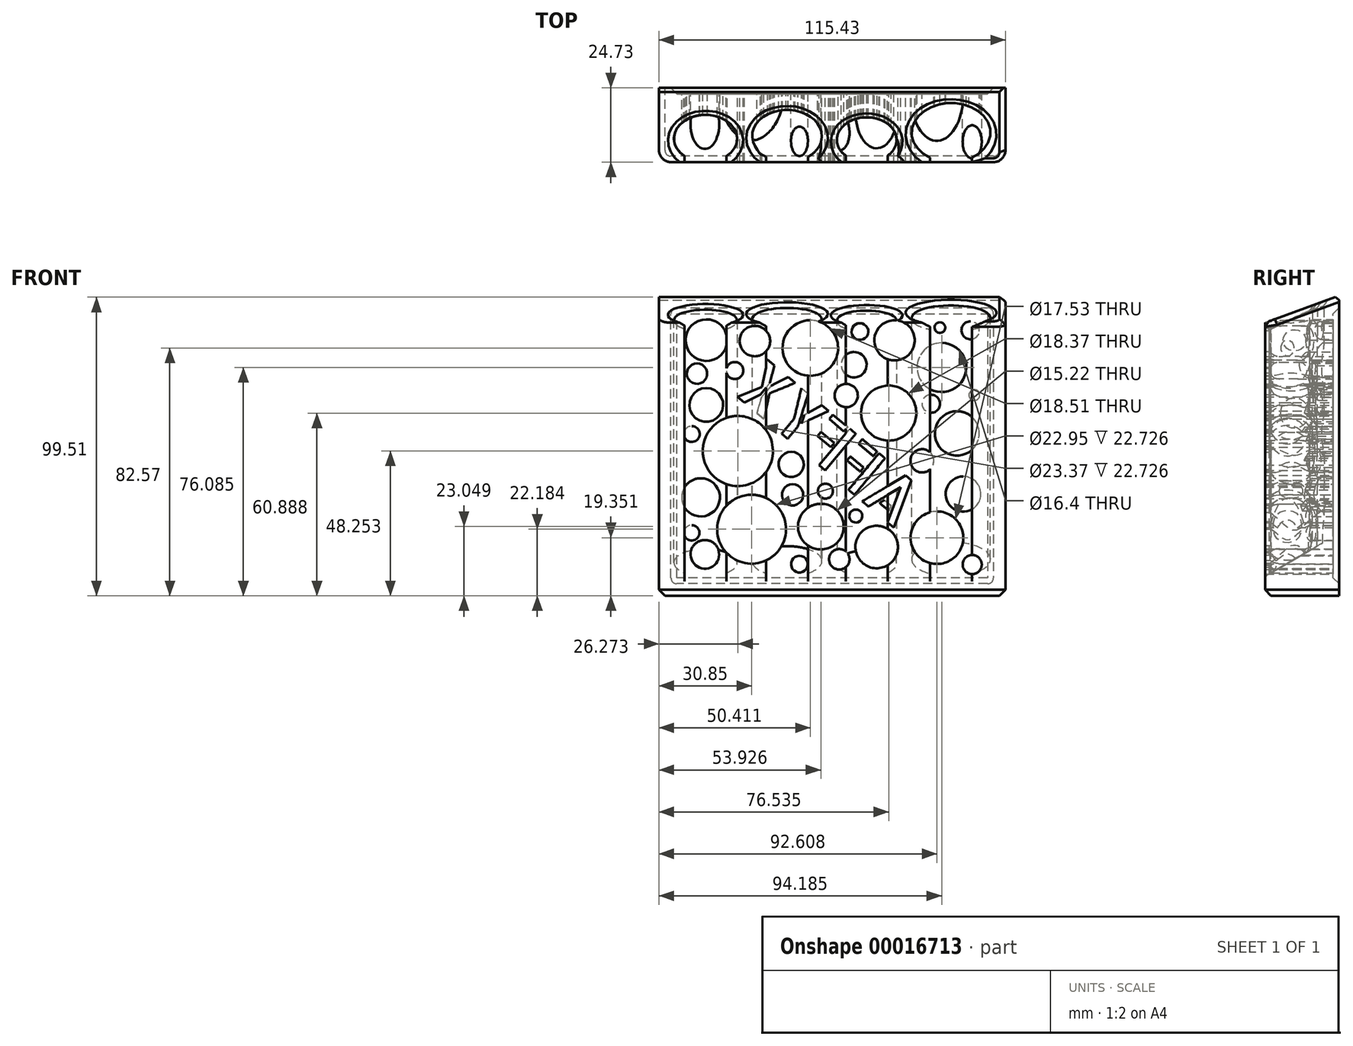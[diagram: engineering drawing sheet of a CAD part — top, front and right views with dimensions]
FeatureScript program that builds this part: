
annotation { "Feature Type Name" : "Feature", "Feature Type Description" : "" }
export const myFeature = defineFeature(function(context is Context, id is Id, definition is map)
    precondition{}
    {
        {
            var Q0;
            Q0=qCreatedBy(makeId("Top.planeOp"),FACE);
            var sketch = newSketch(context, id + "F0", { "sketchPlane" : qUnion([Q0])});
            skEllipse(sketch, "E0", {"center": v(15.53, 7.9) * mm, "majorRadius": 10.53 * mm, "minorRadius": 7.9 * mm, "majorAxis": v(1, 0)});
            skEllipse(sketch, "E1", {"center": v(42.66, 8.7) * mm, "majorRadius": 11.6 * mm, "minorRadius": 8.7 * mm, "majorAxis": v(1, 0)});
            skEllipse(sketch, "E2", {"center": v(69.22, 7.47) * mm, "majorRadius": 9.96 * mm, "minorRadius": 7.47 * mm, "majorAxis": v(-1, 0)});
            skEllipse(sketch, "E3", {"center": v(97.3, 9.85) * mm, "majorRadius": 13.13 * mm, "minorRadius": 9.85 * mm, "majorAxis": v(-1, 0)});
            skLineSegment(sketch, "E4", {"start": v(0, 0) * mm, "end": v(120, 0) * mm, "construction": true});
            skSolve(sketch);
        }
        {
            var Q0;
            Q0=qCreatedBy(makeId("Top.planeOp"),FACE);
            var sketch = newSketch(context, id + "F1", { "sketchPlane" : qUnion([Q0])});
            skLineSegment(sketch, "E5.bottom", {"start": v(8.53, -4.1) * mm, "end": v(22.52, -4.1) * mm});
            skLineSegment(sketch, "E5.top", {"start": v(8.53, 7.9) * mm, "end": v(22.52, 7.9) * mm});
            skLineSegment(sketch, "E5.left", {"start": v(8.53, -4.1) * mm, "end": v(8.53, 7.9) * mm});
            skLineSegment(sketch, "E5.right", {"start": v(22.53, -4.1) * mm, "end": v(22.53, 7.9) * mm});
            skLineSegment(sketch, "E6.bottom", {"start": v(35.66, -3.3) * mm, "end": v(49.66, -3.3) * mm});
            skLineSegment(sketch, "E6.top", {"start": v(35.66, 8.7) * mm, "end": v(49.66, 8.7) * mm});
            skLineSegment(sketch, "E6.left", {"start": v(35.66, -3.3) * mm, "end": v(35.66, 8.7) * mm});
            skLineSegment(sketch, "E6.right", {"start": v(49.66, -3.3) * mm, "end": v(49.66, 8.7) * mm});
            skLineSegment(sketch, "E7.bottom", {"start": v(62.22, -4.53) * mm, "end": v(76.22, -4.53) * mm});
            skLineSegment(sketch, "E7.top", {"start": v(62.22, 7.47) * mm, "end": v(76.22, 7.47) * mm});
            skLineSegment(sketch, "E7.left", {"start": v(62.22, -4.53) * mm, "end": v(62.22, 7.47) * mm});
            skLineSegment(sketch, "E7.right", {"start": v(76.22, -4.53) * mm, "end": v(76.22, 7.47) * mm});
            skLineSegment(sketch, "E8.bottom", {"start": v(90.3, -2.15) * mm, "end": v(104.3, -2.15) * mm});
            skLineSegment(sketch, "E8.top", {"start": v(90.3, 9.85) * mm, "end": v(104.3, 9.85) * mm});
            skLineSegment(sketch, "E8.left", {"start": v(90.3, -2.15) * mm, "end": v(90.3, 9.85) * mm});
            skLineSegment(sketch, "E8.right", {"start": v(104.3, -2.15) * mm, "end": v(104.3, 9.85) * mm});
            skSolve(sketch);
        }
        {
            var Q0;
            Q0=qCreatedBy(makeId("Top.planeOp"),FACE);
            var sketch = newSketch(context, id + "F2", { "sketchPlane" : qUnion([Q0])});
            skLineSegment(sketch, "E9.bottom", {"start": v(0, 0) * mm, "end": v(115.43, 0) * mm});
            skLineSegment(sketch, "E9.top", {"start": v(0, 24.73) * mm, "end": v(115.43, 24.73) * mm});
            skLineSegment(sketch, "E9.left", {"start": v(0, 0) * mm, "end": v(0, 24.73) * mm});
            skLineSegment(sketch, "E9.right", {"start": v(115.43, 0) * mm, "end": v(115.43, 24.73) * mm});
            skSolve(sketch);
        }
        {
            var Q0;
            Q0=makeQuery(id+"F2.imprint","IMPRINT",FACE,{"disambiguationData":[TD([[makeQuery(id+"F2.imprint","IMPRINT",EDGE,{"derivedFrom":sQuery(id+"F2.wireOp",EDGE,"E9.bottom")}),1.0]])]});
            extrude(context, id + "F3", {"entities" : qUnion([Q0]), "oppositeDirection" : true, "depth" : 100 * mm});
        }
        {
            var Q0;
            Q0 = qSketchRegion(id + "F1", true);
            extrude(context, id + "F4", {"entities" : qUnion([Q0]), "operationType" : NewBodyOperationType.REMOVE, "oppositeDirection" : true, "depth" : 95 * mm});
        }
        {
            var Q0;
            Q0 = qSketchRegion(id + "F0", true);
            extrude(context, id + "F5", {"entities" : qUnion([Q0]), "operationType" : NewBodyOperationType.REMOVE, "oppositeDirection" : true, "depth" : 95 * mm});
        }
        {
            var Q0;
            Q0=makeQuery(id+"F3.opExtrude","SWEPT_FACE",FACE,{"disambiguationData":[OSD([sQuery(id+"F2.wireOp",EDGE,"E9.right")])]});
            var sketch = newSketch(context, id + "F6", { "sketchPlane" : qUnion([Q0])});
            skLineSegment(sketch, "E10", {"start": v(0, -100) * mm, "end": v(0, -93.5) * mm});
            skLineSegment(sketch, "E11", {"start": v(0, -93.5) * mm, "end": v(24.73, -79.22) * mm});
            skLineSegment(sketch, "E12", {"start": v(24.73, -79.22) * mm, "end": v(24.73, -100) * mm});
            skLineSegment(sketch, "E13", {"start": v(24.73, -100) * mm, "end": v(0, -100) * mm});
            skSolve(sketch);
        }
        {
            var Q0;
            Q0 = qSketchRegion(id + "F6", true);
            var Q1;
            Q1=makeQuery(id+"F3.opExtrude","SWEPT_FACE",FACE,{"disambiguationData":[OSD([sQuery(id+"F2.wireOp",EDGE,"E9.left")])]});
            extrude(context, id + "F7", {"entities" : qUnion([Q0]), "operationType" : NewBodyOperationType.ADD, "endBound" : BoundingType.UP_TO_SURFACE, "oppositeDirection" : true, "endBoundEntityFace" : qUnion([Q1]), "depth" : 25 * mm});
        }
        {
            var Q0;
            Q0=makeQuery(id+"F3.opExtrude","SWEPT_FACE",FACE,{"disambiguationData":[OSD([sQuery(id+"F2.wireOp",EDGE,"E9.left")])]});
            var sketch = newSketch(context, id + "F8", { "sketchPlane" : qUnion([Q0])});
            skLineSegment(sketch, "E14", {"start": v(0, 0) * mm, "end": v(-24.73, 0) * mm});
            skLineSegment(sketch, "E15", {"start": v(-24.73, 0) * mm, "end": v(0, -9) * mm});
            skLineSegment(sketch, "E16", {"start": v(0, -9) * mm, "end": v(0, 0) * mm});
            skSolve(sketch);
        }
        {
            var Q0;
            Q0=makeQuery(id+"F8.imprint","IMPRINT",FACE,{"disambiguationData":[TD([[makeQuery(id+"F8.imprint","IMPRINT",EDGE,{"derivedFrom":sQuery(id+"F8.wireOp",EDGE,"E14")}),1.0]])]});
            extrude(context, id + "F9", {"entities" : qUnion([Q0]), "operationType" : NewBodyOperationType.REMOVE, "endBound" : BoundingType.THROUGH_ALL, "oppositeDirection" : true, "depth" : 25 * mm});
        }
        {
            var Q0;
            Q0=makeQuery(id+"F3.opExtrude","SWEPT_EDGE",EDGE,{"disambiguationData":[OSD([sQuery(id+"F2.wireOp",EDGE,"E9.bottom"),sQuery(id+"F2.wireOp",EDGE,"E9.right")])]});
            var Q1;
            Q1=makeQuery(id+"F9.boolean.opBoolean","COPY",EDGE,{"disambiguationData":[OD(1.0)],"derivedFrom":makeQuery(id+"F9.opExtrude","SWEPT_EDGE",EDGE,{"disambiguationData":[OSD([sQuery(id+"F2.wireOp",EDGE,"E9.bottom"),sQuery(id+"F2.wireOp",EDGE,"E9.left"),sQuery(id+"F8.wireOp",EDGE,"E15"),sQuery(id+"F8.wireOp",EDGE,"E16")])]})});
            var Q2;
            Q2=makeQuery(id+"F9.boolean.opBoolean","COPY",EDGE,{"disambiguationData":[OD(4.0)],"derivedFrom":makeQuery(id+"F9.opExtrude","SWEPT_EDGE",EDGE,{"disambiguationData":[OSD([sQuery(id+"F2.wireOp",EDGE,"E9.bottom"),sQuery(id+"F2.wireOp",EDGE,"E9.left"),sQuery(id+"F8.wireOp",EDGE,"E15"),sQuery(id+"F8.wireOp",EDGE,"E16")])]})});
            var Q3;
            Q3=makeQuery(id+"F9.boolean.opBoolean","COPY",EDGE,{"disambiguationData":[OD(3.0)],"derivedFrom":makeQuery(id+"F9.opExtrude","SWEPT_EDGE",EDGE,{"disambiguationData":[OSD([sQuery(id+"F2.wireOp",EDGE,"E9.bottom"),sQuery(id+"F2.wireOp",EDGE,"E9.left"),sQuery(id+"F8.wireOp",EDGE,"E15"),sQuery(id+"F8.wireOp",EDGE,"E16")])]})});
            var Q4;
            Q4=makeQuery(id+"F9.boolean.opBoolean","COPY",EDGE,{"disambiguationData":[OD(2.0)],"derivedFrom":makeQuery(id+"F9.opExtrude","SWEPT_EDGE",EDGE,{"disambiguationData":[OSD([sQuery(id+"F2.wireOp",EDGE,"E9.bottom"),sQuery(id+"F2.wireOp",EDGE,"E9.left"),sQuery(id+"F8.wireOp",EDGE,"E15"),sQuery(id+"F8.wireOp",EDGE,"E16")])]})});
            var Q5;
            Q5=makeQuery(id+"F9.boolean.opBoolean","COPY",EDGE,{"disambiguationData":[OD(0.0)],"derivedFrom":makeQuery(id+"F9.opExtrude","SWEPT_EDGE",EDGE,{"disambiguationData":[OSD([sQuery(id+"F2.wireOp",EDGE,"E9.bottom"),sQuery(id+"F2.wireOp",EDGE,"E9.left"),sQuery(id+"F8.wireOp",EDGE,"E15"),sQuery(id+"F8.wireOp",EDGE,"E16")])]})});
            var Q6;
            Q6=makeQuery(id+"F3.opExtrude","SWEPT_EDGE",EDGE,{"disambiguationData":[OSD([sQuery(id+"F2.wireOp",EDGE,"E9.bottom"),sQuery(id+"F2.wireOp",EDGE,"E9.left")])]});
            fillet(context, id + "F10", {"entities" : qUnion([Q0, Q1, Q2, Q3, Q4, Q5, Q6]), "radius" : 4 * mm, "allowEdgeOverflow" : false});
        }
        {
            var Q0;
            Q0=makeQuery(id+"F9.boolean.opBoolean","COPY",EDGE,{"derivedFrom":makeQuery(id+"F9.opExtrude","CAP_EDGE",EDGE,{"disambiguationData":[OSD([sQuery(id+"F8.wireOp",EDGE,"E15")])],"isStart":true})});
            var Q1;
            Q1=makeQuery(id+"F9.boolean.opBoolean","INTERSECT",EDGE,{"derivedFrom":[makeQuery(id+"F3.opExtrude","SWEPT_FACE",FACE,{"disambiguationData":[OSD([sQuery(id+"F2.wireOp",EDGE,"E9.right")])]}),makeQuery(id+"F9.opExtrude","SWEPT_FACE",FACE,{"disambiguationData":[OSD([sQuery(id+"F8.wireOp",EDGE,"E15")])]})]});
            var Q2;
            Q2=makeQuery(id+"F3.opExtrude","CAP_EDGE",EDGE,{"disambiguationData":[OSD([sQuery(id+"F2.wireOp",EDGE,"E9.bottom")])],"isStart":false});
            var Q3;
            Q3=makeQuery(id+"F9.boolean.opBoolean","INTERSECT",EDGE,{"derivedFrom":[makeQuery(id+"F5.boolean.opBoolean","COPY",FACE,{"derivedFrom":makeQuery(id+"F5.opExtrude","SWEPT_FACE",FACE,{"disambiguationData":[OSD([sQuery(id+"F0.wireOp",EDGE,"E1")])]})}),makeQuery(id+"F9.opExtrude","SWEPT_FACE",FACE,{"disambiguationData":[OSD([sQuery(id+"F8.wireOp",EDGE,"E15")])]})]});
            var Q4;
            Q4=makeQuery(id+"F9.boolean.opBoolean","INTERSECT",EDGE,{"derivedFrom":[makeQuery(id+"F5.boolean.opBoolean","COPY",FACE,{"derivedFrom":makeQuery(id+"F5.opExtrude","SWEPT_FACE",FACE,{"disambiguationData":[OSD([sQuery(id+"F0.wireOp",EDGE,"E2")])]})}),makeQuery(id+"F9.opExtrude","SWEPT_FACE",FACE,{"disambiguationData":[OSD([sQuery(id+"F8.wireOp",EDGE,"E15")])]})]});
            var Q5;
            Q5=makeQuery(id+"F9.boolean.opBoolean","INTERSECT",EDGE,{"derivedFrom":[makeQuery(id+"F5.boolean.opBoolean","COPY",FACE,{"derivedFrom":makeQuery(id+"F5.opExtrude","SWEPT_FACE",FACE,{"disambiguationData":[OSD([sQuery(id+"F0.wireOp",EDGE,"E3")])]})}),makeQuery(id+"F9.opExtrude","SWEPT_FACE",FACE,{"disambiguationData":[OSD([sQuery(id+"F8.wireOp",EDGE,"E15")])]})]});
            var Q6;
            Q6=makeQuery(id+"F9.boolean.opBoolean","INTERSECT",EDGE,{"derivedFrom":[makeQuery(id+"F5.boolean.opBoolean","COPY",FACE,{"derivedFrom":makeQuery(id+"F5.opExtrude","SWEPT_FACE",FACE,{"disambiguationData":[OSD([sQuery(id+"F0.wireOp",EDGE,"E0")])]})}),makeQuery(id+"F9.opExtrude","SWEPT_FACE",FACE,{"disambiguationData":[OSD([sQuery(id+"F8.wireOp",EDGE,"E15")])]})]});
            chamfer(context, id + "F11", {"entities" : qUnion([Q0, Q1, Q2, Q3, Q4, Q5, Q6]), "width" : 2 * mm, "tangentPropagation" : true});
        }
        {
            var Q0;
            {var subQ0=sQuery(id+"F6.wireOp",EDGE,"E10");var subQ1=sQuery(id+"F2.wireOp",EDGE,"E9.bottom");var subQ2=sQuery(id+"F6.wireOp",EDGE,"E11");Q0=makeQuery(id+"F7.boolean.opBoolean","SPLIT",EDGE,{"disambiguationData":[TD([makeQuery(id+"F4.boolean.opBoolean","COPY",FACE,{"derivedFrom":makeQuery(id+"F4.opExtrude","SWEPT_FACE",FACE,{"disambiguationData":[OSD([sQuery(id+"F1.wireOp",EDGE,"E5.left")])]})})])],"derivedFrom":makeQuery(id+"F7.opExtrude","SWEPT_EDGE",EDGE,{"disambiguationData":[OSD([subQ1,sQuery(id+"F2.wireOp",EDGE,"E9.right"),subQ0,subQ2])]})});}
            var Q1;
            {var subQ0=sQuery(id+"F6.wireOp",EDGE,"E10");var subQ1=sQuery(id+"F2.wireOp",EDGE,"E9.bottom");var subQ2=sQuery(id+"F6.wireOp",EDGE,"E11");Q1=makeQuery(id+"F7.boolean.opBoolean","SPLIT",EDGE,{"disambiguationData":[TD([makeQuery(id+"F4.boolean.opBoolean","COPY",FACE,{"derivedFrom":makeQuery(id+"F4.opExtrude","SWEPT_FACE",FACE,{"disambiguationData":[OSD([sQuery(id+"F1.wireOp",EDGE,"E6.left")])]})})])],"derivedFrom":makeQuery(id+"F7.opExtrude","SWEPT_EDGE",EDGE,{"disambiguationData":[OSD([subQ1,sQuery(id+"F2.wireOp",EDGE,"E9.right"),subQ0,subQ2])]})});}
            var Q2;
            {var subQ0=sQuery(id+"F6.wireOp",EDGE,"E10");var subQ1=sQuery(id+"F6.wireOp",EDGE,"E11");var subQ2=sQuery(id+"F2.wireOp",EDGE,"E9.bottom");Q2=makeQuery(id+"F7.boolean.opBoolean","SPLIT",EDGE,{"disambiguationData":[TD([makeQuery(id+"F4.boolean.opBoolean","COPY",FACE,{"derivedFrom":makeQuery(id+"F4.opExtrude","SWEPT_FACE",FACE,{"disambiguationData":[OSD([sQuery(id+"F1.wireOp",EDGE,"E7.left")])]})})])],"derivedFrom":makeQuery(id+"F7.opExtrude","SWEPT_EDGE",EDGE,{"disambiguationData":[OSD([subQ2,sQuery(id+"F2.wireOp",EDGE,"E9.right"),subQ0,subQ1])]})});}
            var Q3;
            {var subQ0=sQuery(id+"F6.wireOp",EDGE,"E10");var subQ1=sQuery(id+"F2.wireOp",EDGE,"E9.bottom");var subQ2=sQuery(id+"F6.wireOp",EDGE,"E11");Q3=makeQuery(id+"F7.boolean.opBoolean","SPLIT",EDGE,{"disambiguationData":[TD([makeQuery(id+"F4.boolean.opBoolean","COPY",FACE,{"derivedFrom":makeQuery(id+"F4.opExtrude","SWEPT_FACE",FACE,{"disambiguationData":[OSD([sQuery(id+"F1.wireOp",EDGE,"E8.left")])]})})])],"derivedFrom":makeQuery(id+"F7.opExtrude","SWEPT_EDGE",EDGE,{"disambiguationData":[OSD([subQ1,sQuery(id+"F2.wireOp",EDGE,"E9.right"),subQ0,subQ2])]})});}
            fillet(context, id + "F12", {"entities" : qUnion([Q0, Q1, Q2, Q3]), "radius" : 3 * mm, "rho" : .75, "crossSection" : FilletCrossSection.CONIC, "allowEdgeOverflow" : false});
        }
        {
            var Q0;
            Q0=makeQuery(id+"F3.opExtrude","SWEPT_FACE",FACE,{"disambiguationData":[OSD([sQuery(id+"F2.wireOp",EDGE,"E9.top")])]});
            var sketch = newSketch(context, id + "F13", { "sketchPlane" : qUnion([Q0])});
            skLineSegment(sketch, "E17.0", {"start": v(-109.43, -96) * mm, "end": v(-6, -96) * mm});
            skLineSegment(sketch, "E17.1", {"start": v(-111.43, -6) * mm, "end": v(-111.43, -94) * mm});
            skLineSegment(sketch, "E17.2", {"start": v(-6, -4) * mm, "end": v(-109.43, -4) * mm});
            skLineSegment(sketch, "E17.3", {"start": v(-4, -94) * mm, "end": v(-4, -6) * mm});
            skPoint(sketch, "E18.visualSharp", {"position": v(-111.43, -4) * mm});
            skArc(sketch, "E18.filletArc", {"start": v(-109.43, -4) * mm, "mid": v(-110.84, -4.59) * mm, "end": v(-111.43, -6) * mm});
            skPoint(sketch, "E19.visualSharp", {"position": v(-4, -4) * mm});
            skArc(sketch, "E19.filletArc", {"start": v(-4, -6) * mm, "mid": v(-4.59, -4.59) * mm, "end": v(-6, -4) * mm});
            skPoint(sketch, "E20.visualSharp", {"position": v(-4, -96) * mm});
            skArc(sketch, "E20.filletArc", {"start": v(-6, -96) * mm, "mid": v(-4.59, -95.41) * mm, "end": v(-4, -94) * mm});
            skPoint(sketch, "E21.visualSharp", {"position": v(-111.43, -96) * mm});
            skArc(sketch, "E21.filletArc", {"start": v(-111.43, -94) * mm, "mid": v(-110.84, -95.41) * mm, "end": v(-109.43, -96) * mm});
            skSolve(sketch);
        }
        {
            var Q0;
            Q0=makeQuery(id+"F13.imprint","IMPRINT",FACE,{"disambiguationData":[TD([[makeQuery(id+"F13.imprint","IMPRINT",EDGE,{"derivedFrom":sQuery(id+"F13.wireOp",EDGE,"E17.0")}),1.0]])]});
            extrude(context, id + "F14", {"entities" : qUnion([Q0]), "operationType" : NewBodyOperationType.REMOVE, "oppositeDirection" : true, "depth" : 2 * mm, "hasDraft" : true, "draftAngle" : 45 * degree, "draftPullDirection" : true});
        }
        {
            var Q0;
            Q0=makeQuery(id+"F14.boolean.opBoolean","COPY",FACE,{"derivedFrom":makeQuery(id+"F14.opExtrude","CAP_FACE",FACE,{"disambiguationData":[OSD([sQuery(id+"F13.wireOp",EDGE,"E17.0"),sQuery(id+"F13.wireOp",EDGE,"E17.1"),sQuery(id+"F13.wireOp",EDGE,"E17.2"),sQuery(id+"F13.wireOp",EDGE,"E17.3"),sQuery(id+"F13.wireOp",EDGE,"E18.filletArc"),sQuery(id+"F13.wireOp",EDGE,"E19.filletArc"),sQuery(id+"F13.wireOp",EDGE,"E20.filletArc"),sQuery(id+"F13.wireOp",EDGE,"E21.filletArc")])],"isStart":false})});
            var sketch = newSketch(context, id + "F15", { "sketchPlane" : qUnion([Q0])});
            skText(sketch, "E22", { "text": "AFFYX", "fontName": "AllertaStencil-Regular.ttf"});
            skCircle(sketch, "E23", {"center": v(-94.18, -23.92) * mm, "radius": 8.2 * mm});
            skCircle(sketch, "E24", {"center": v(-64.93, -23) * mm, "radius": 4.24 * mm});
            skCircle(sketch, "E25", {"center": v(-76.54, -39.11) * mm, "radius": 9.19 * mm});
            skCircle(sketch, "E26", {"center": v(-99.28, -45.88) * mm, "radius": 7.4 * mm});
            skCircle(sketch, "E27", {"center": v(-90.64, -36) * mm, "radius": 3 * mm});
            skCircle(sketch, "E28", {"center": v(-78.47, -14.87) * mm, "radius": 6.7 * mm});
            skCircle(sketch, "E29", {"center": v(-103.76, -11.52) * mm, "radius": 3 * mm});
            skCircle(sketch, "E30", {"center": v(-50.41, -17.43) * mm, "radius": 9.26 * mm});
            skCircle(sketch, "E31", {"center": v(-62.37, -33.27) * mm, "radius": 3.87 * mm});
            skCircle(sketch, "E32", {"center": v(-87.66, -55.02) * mm, "radius": 3.9 * mm});
            skCircle(sketch, "E33", {"center": v(-101.37, -66.09) * mm, "radius": 5.85 * mm});
            skCircle(sketch, "E34", {"center": v(-92.6, -80.65) * mm, "radius": 8.76 * mm});
            skCircle(sketch, "E35", {"center": v(-104.33, -89.59) * mm, "radius": 3.18 * mm});
            skCircle(sketch, "E36", {"center": v(-31.94, -15.12) * mm, "radius": 5.08 * mm});
            skCircle(sketch, "E37", {"center": v(-15.8, -14.81) * mm, "radius": 6.94 * mm});
            skCircle(sketch, "E38", {"center": v(-25.26, -24.94) * mm, "radius": 2.85 * mm});
            skCircle(sketch, "E39", {"center": v(-15.77, -36.39) * mm, "radius": 5.63 * mm});
            skCircle(sketch, "E40", {"center": v(-12.67, -25.98) * mm, "radius": 3.4 * mm});
            skCircle(sketch, "E41", {"center": v(-26.27, -51.75) * mm, "radius": 11.68 * mm});
            skCircle(sketch, "E42", {"center": v(-10.93, -46.1) * mm, "radius": 2.63 * mm});
            skCircle(sketch, "E43", {"center": v(-13.93, -67.2) * mm, "radius": 6.37 * mm});
            skCircle(sketch, "E44", {"center": v(-53.93, -76.95) * mm, "radius": 7.61 * mm});
            skCircle(sketch, "E45", {"center": v(-44.51, -66.34) * mm, "radius": 3.56 * mm});
            skCircle(sketch, "E46", {"center": v(-44.05, -56.22) * mm, "radius": 4.21 * mm});
            skCircle(sketch, "E47", {"center": v(-55.45, -65.13) * mm, "radius": 2.5 * mm});
            skCircle(sketch, "E48", {"center": v(-72.5, -83.75) * mm, "radius": 7.08 * mm});
            skCircle(sketch, "E49", {"center": v(-65.57, -73.41) * mm, "radius": 2.17 * mm});
            skCircle(sketch, "E50", {"center": v(-30.85, -77.82) * mm, "radius": 11.48 * mm});
            skCircle(sketch, "E51", {"center": v(-15.29, -86.2) * mm, "radius": 4.8 * mm});
            skCircle(sketch, "E52", {"center": v(-10.91, -79.02) * mm, "radius": 2.57 * mm});
            skCircle(sketch, "E53", {"center": v(-60.07, -87.84) * mm, "radius": 3.41 * mm});
            skCircle(sketch, "E54", {"center": v(-46.8, -89.49) * mm, "radius": 2.83 * mm});
            skCircle(sketch, "E55", {"center": v(-105.06, -33.12) * mm, "radius": 1.8 * mm});
            skCircle(sketch, "E56", {"center": v(-66.93, -11.94) * mm, "radius": 2.8 * mm});
            skCircle(sketch, "E57", {"center": v(-93.59, -10.62) * mm, "radius": 1.8 * mm});
            const initialGuessF15  = {"E22": [-0.07922, -0.07817, 0.76604, 0.64279, 0.01588]};
            skSetInitialGuess(sketch, initialGuessF15);
            skSolve(sketch);
        }
        {
            var Q0;
            Q0 = qSketchRegion(id + "F15", true);
            extrude(context, id + "F16", {"entities" : qUnion([Q0]), "operationType" : NewBodyOperationType.REMOVE, "endBound" : BoundingType.UP_TO_NEXT, "oppositeDirection" : true, "depth" : 25 * mm});
        }
        {
            var Q0;
            {var subQ0=sQuery(id+"F2.wireOp",EDGE,"E9.top");Q0=makeQuery(id+"F9.boolean.opBoolean","MERGE",EDGE,{"derivedFrom":[makeQuery(id+"F3.opExtrude","CAP_EDGE",EDGE,{"disambiguationData":[OSD([subQ0])],"isStart":true}),makeQuery(id+"F9.opExtrude","SWEPT_EDGE",EDGE,{"disambiguationData":[OSD([subQ0,sQuery(id+"F2.wireOp",EDGE,"E9.left"),sQuery(id+"F8.wireOp",EDGE,"E14"),sQuery(id+"F8.wireOp",EDGE,"E15")])]})]});}
            chamfer(context, id + "F17", {"entities" : qUnion([Q0]), "width" : 1 * mm, "tangentPropagation" : true});
        }
    });
